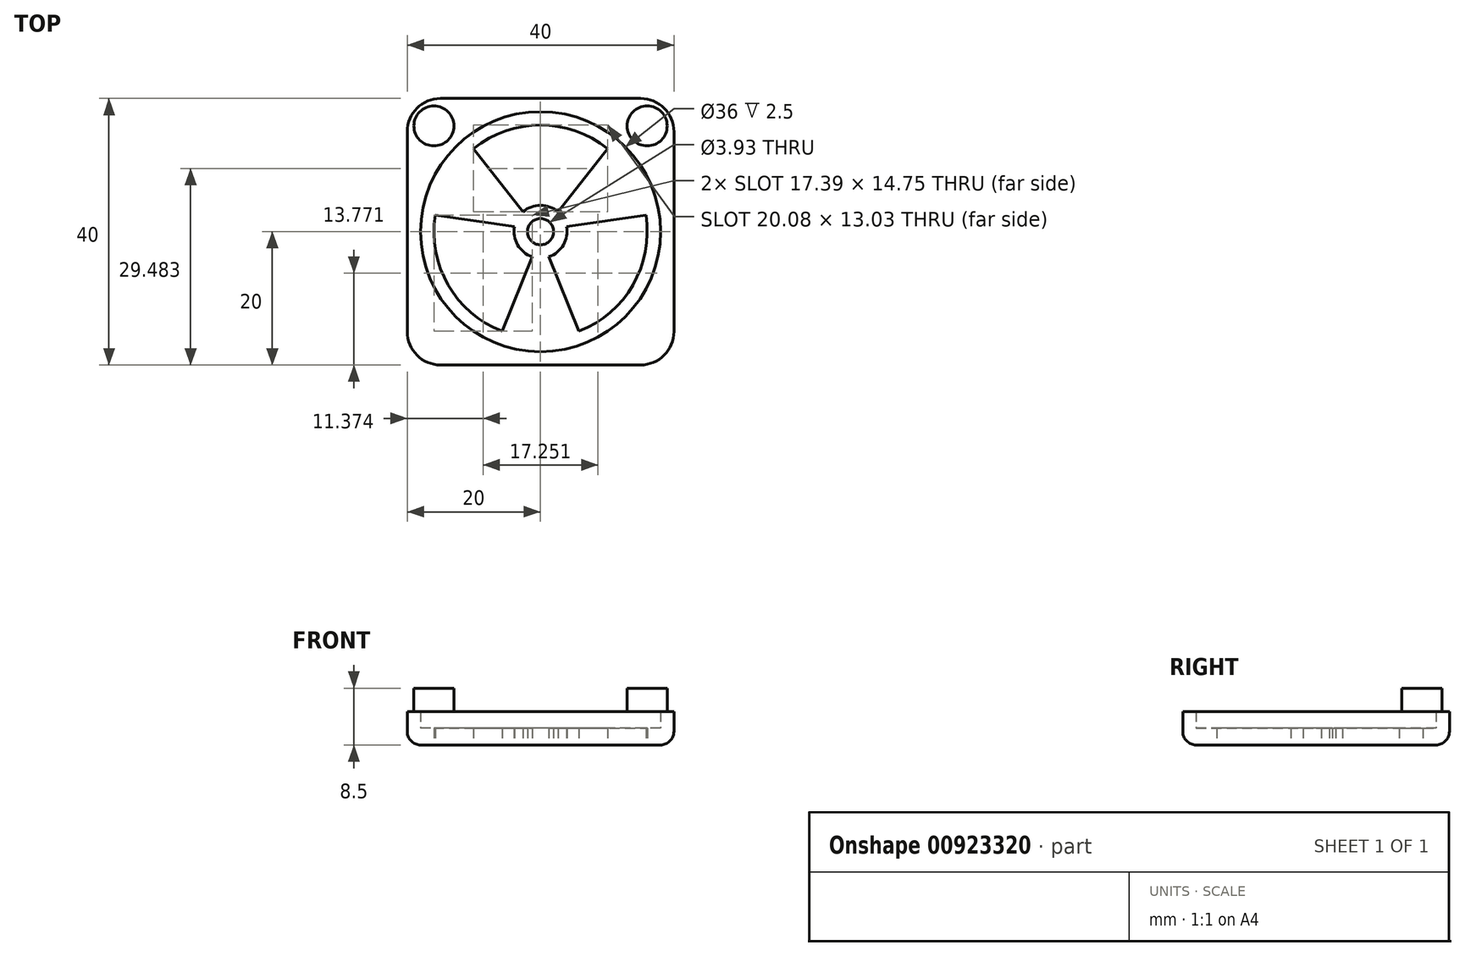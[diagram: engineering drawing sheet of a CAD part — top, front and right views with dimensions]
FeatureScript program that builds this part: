
annotation { "Feature Type Name" : "Feature", "Feature Type Description" : "" }
export const myFeature = defineFeature(function(context is Context, id is Id, definition is map)
    precondition{}
    {
        {
            var Q0;
            Q0=qCreatedBy(makeId("Top.planeOp"),FACE);
            var sketch = newSketch(context, id + "F0", { "sketchPlane" : qUnion([Q0])});
            skLineSegment(sketch, "E0.bottom", {"start": v(20, 20) * mm, "end": v(-20, 20) * mm});
            skLineSegment(sketch, "E0.top", {"start": v(20, -20) * mm, "end": v(-20, -20) * mm});
            skLineSegment(sketch, "E0.left", {"start": v(20, 20) * mm, "end": v(20, -20) * mm});
            skLineSegment(sketch, "E0.right", {"start": v(-20, 20) * mm, "end": v(-20, -20) * mm});
            skPoint(sketch, "E0.middle", {"position": v(0, 0) * mm});
            skCircle(sketch, "E1", {"center": v(0, 0) * mm, "radius": 18 * mm});
            skCircle(sketch, "E2", {"center": v(-16, 15.87) * mm, "radius": 3 * mm});
            skCircle(sketch, "E3", {"center": v(16, 15.87) * mm, "radius": 3 * mm});
            skCircle(sketch, "E4", {"center": v(0, 0) * mm, "radius": 16 * mm});
            skCircle(sketch, "E5", {"center": v(0, 0) * mm, "radius": 3.96 * mm});
            skCircle(sketch, "E6", {"center": v(0, 0) * mm, "radius": 1.96 * mm});
            skLineSegment(sketch, "E7", {"start": v(-5.77, -14.92) * mm, "end": v(-1.25, -3.76) * mm});
            skLineSegment(sketch, "E8", {"start": v(1.25, -3.76) * mm, "end": v(5.77, -14.92) * mm});
            skLineSegment(sketch, "E9.1.0", {"start": v(2.63, 2.97) * mm, "end": v(10.04, 12.46) * mm});
            skLineSegment(sketch, "E9.1.1", {"start": v(15.8, 2.47) * mm, "end": v(3.88, 0.8) * mm});
            skLineSegment(sketch, "E9.2.0", {"start": v(-3.88, 0.8) * mm, "end": v(-15.8, 2.47) * mm});
            skLineSegment(sketch, "E9.2.1", {"start": v(-10.04, 12.46) * mm, "end": v(-2.63, 2.97) * mm});
            skLineSegment(sketch, "E10", {"start": v(-23.55, 15.87) * mm, "end": v(21.4, 15.87) * mm, "construction": true});
            skSolve(sketch);
        }
        {
            var Q0;
            Q0=makeQuery(id+"F0.imprint","IMPRINT",FACE,{"disambiguationData":[TD([[makeQuery(id+"F0.imprint","IMPRINT",EDGE,{"derivedFrom":sQuery(id+"F0.wireOp",EDGE,"E0.bottom")}),1.0]])]});
            extrude(context, id + "F1", {"entities" : qUnion([Q0]), "depth" : 5 * mm, "offsetDistance" : 25 * mm});
        }
        {
            var Q0;
            Q0=makeQuery(id+"F0.imprint","IMPRINT",FACE,{"disambiguationData":[TD([[makeQuery(id+"F0.imprint","IMPRINT",EDGE,{"derivedFrom":sQuery(id+"F0.wireOp",EDGE,"E2")}),1.0]])]});
            var Q1;
            Q1=makeQuery(id+"F0.imprint","IMPRINT",FACE,{"disambiguationData":[TD([[makeQuery(id+"F0.imprint","IMPRINT",EDGE,{"derivedFrom":sQuery(id+"F0.wireOp",EDGE,"E3")}),1.0]])]});
            extrude(context, id + "F2", {"entities" : qUnion([Q0, Q1]), "operationType" : NewBodyOperationType.ADD, "depth" : 8.5 * mm, "offsetDistance" : 25 * mm});
        }
        {
            var Q0;
            Q0=makeQuery(id+"F1.opExtrude","SWEPT_EDGE",EDGE,{"disambiguationData":[OSD([sQuery(id+"F0.wireOp",EDGE,"E0.top"),sQuery(id+"F0.wireOp",EDGE,"E0.right")])]});
            var Q1;
            Q1=makeQuery(id+"F1.opExtrude","SWEPT_EDGE",EDGE,{"disambiguationData":[OSD([sQuery(id+"F0.wireOp",EDGE,"E0.bottom"),sQuery(id+"F0.wireOp",EDGE,"E0.right")])]});
            var Q2;
            Q2=makeQuery(id+"F1.opExtrude","SWEPT_EDGE",EDGE,{"disambiguationData":[OSD([sQuery(id+"F0.wireOp",EDGE,"E0.top"),sQuery(id+"F0.wireOp",EDGE,"E0.left")])]});
            var Q3;
            Q3=makeQuery(id+"F1.opExtrude","SWEPT_EDGE",EDGE,{"disambiguationData":[OSD([sQuery(id+"F0.wireOp",EDGE,"E0.bottom"),sQuery(id+"F0.wireOp",EDGE,"E0.left")])]});
            fillet(context, id + "F3", {"entities" : qUnion([Q0, Q1, Q2, Q3]), "radius" : 5 * mm, "tangentPropagation" : true, "allowEdgeOverflow" : false});
        }
        {
            var Q0;
            Q0=makeQuery(id+"F1.opExtrude","CAP_EDGE",EDGE,{"disambiguationData":[OSD([sQuery(id+"F0.wireOp",EDGE,"E0.left")])],"isStart":true});
            fillet(context, id + "F4", {"entities" : qUnion([Q0]), "radius" : 2 * mm, "tangentPropagation" : true, "allowEdgeOverflow" : false});
        }
        {
            var Q0;
            Q0=makeQuery(id+"F0.imprint","IMPRINT",FACE,{"disambiguationData":[TD([[makeQuery(id+"F0.imprint","IMPRINT",EDGE,{"derivedFrom":sQuery(id+"F0.wireOp",EDGE,"E1")}),1.0]])]});
            var Q1;
            Q1=makeQuery(id+"F0.imprint","IMPRINT",FACE,{"disambiguationData":[TD([[makeQuery(id+"F0.imprint","IMPRINT",EDGE,{"derivedFrom":sQuery(id+"F0.wireOp",EDGE,"E6")}),-1.0]])]});
            var Q2;
            {var subQ0=sQuery(id+"F0.wireOp",EDGE,"E7");Q2=makeQuery(id+"F0.imprint","IMPRINT",FACE,{"disambiguationData":[TD([[makeQuery(id+"F0.imprint","IMPRINT",EDGE,{"derivedFrom":subQ0}),-1.0]])]});}
            var Q3;
            {var subQ0=sQuery(id+"F0.wireOp",EDGE,"E9.1.0");Q3=makeQuery(id+"F0.imprint","IMPRINT",FACE,{"disambiguationData":[TD([[makeQuery(id+"F0.imprint","IMPRINT",EDGE,{"derivedFrom":subQ0}),-1.0]])]});}
            var Q4;
            {var subQ0=sQuery(id+"F0.wireOp",EDGE,"E9.2.0");Q4=makeQuery(id+"F0.imprint","IMPRINT",FACE,{"disambiguationData":[TD([[makeQuery(id+"F0.imprint","IMPRINT",EDGE,{"derivedFrom":subQ0}),-1.0]])]});}
            extrude(context, id + "F5", {"entities" : qUnion([Q0, Q1, Q2, Q3, Q4]), "operationType" : NewBodyOperationType.ADD, "depth" : 2.5 * mm, "offsetDistance" : 25 * mm});
        }
    });
